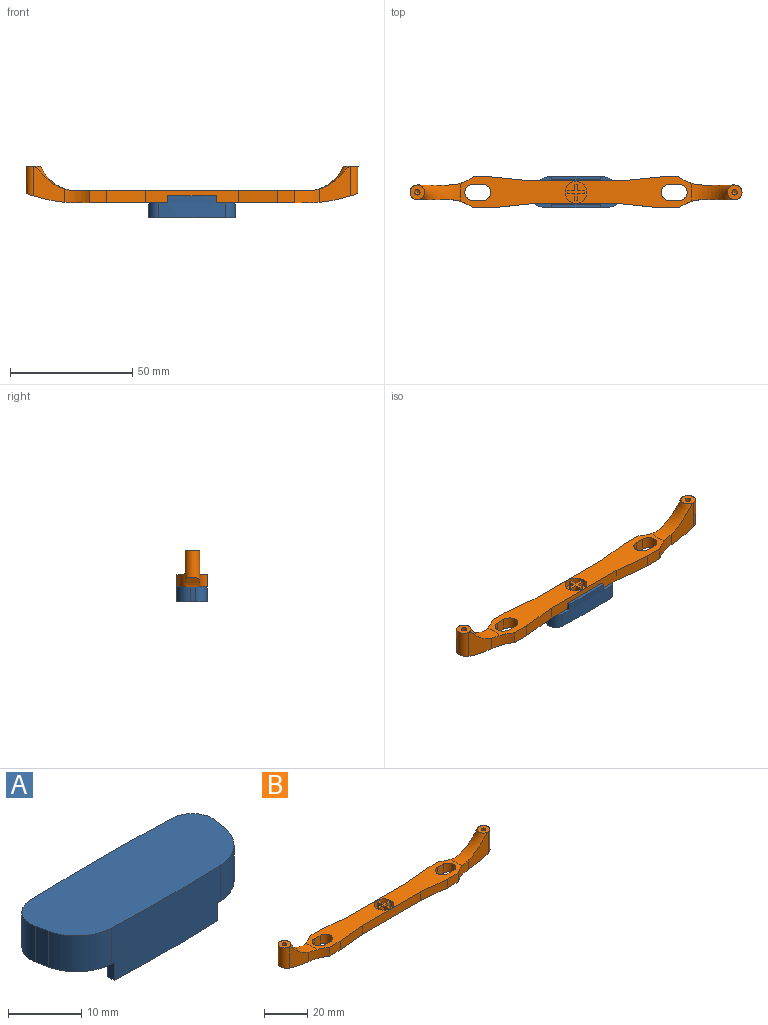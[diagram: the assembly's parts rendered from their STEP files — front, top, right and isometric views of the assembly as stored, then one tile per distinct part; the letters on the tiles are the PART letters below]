
ASSEMBLY  parts=2 mates=1
PART A: 18 faces, bbox 35.3x13x9 mm
  f0: plane 35.26x12.66mm, normal (0,0,-1), area 358.1mm2, adj f1,f2,f3,f4,f5,f6,f7,f8
  f1: plane 6x2.13mm, normal (0.98,-0.2,0), area 13mm2, adj f0,f2,f8,f9
  f2: cylinder r=4mm len=6mm, axis (0,0,-1), area 41.7mm2, adj f0,f1,f3,f9
  f3: cylinder r=342.5mm len=27.58mm, axis (0,0,-1), area 225.5mm2, adj f0,f2,f4,f9,f11,f12,f13
  f4: cylinder r=4mm len=6mm, axis (0,0,-1), area 41.7mm2, adj f0,f3,f5,f9
  f5: plane 6x2.13mm, normal (-0.98,-0.2,0), area 13mm2, adj f0,f4,f6,f9
  f6: cylinder r=7mm len=6.57mm, axis (0,0,-1), area 55.6mm2, adj f0,f5,f7,f9
  f7: cylinder r=256.25mm len=21.07mm, axis (0,0,-1), area 186.5mm2, adj f0,f6,f8,f9,f14,f16,f17
  f8: cylinder r=7mm len=6.57mm, axis (0,0,-1), area 55.6mm2, adj f0,f1,f7,f9
  f9: plane 35.26x13mm, normal (0,0,1), area 415.8mm2, adj f1,f2,f3,f4,f5,f6,f7,f8
  f10: plane 20x3mm, normal (0,-1,0), area 60mm2, adj f0,f11,f12,f13
  f11: plane 3x1.35mm, normal (-1,0,0), area 4.1mm2, adj f0,f3,f10,f13
  f12: plane 3x1.35mm, normal (1,0,0), area 4.1mm2, adj f0,f3,f10,f13
  f13: plane 20x1.5mm, normal (0,0,-1), area 29mm2, adj f3,f10,f11,f12
  f14: plane 3x1.31mm, normal (-1,0,0), area 3.9mm2, adj f0,f7,f15,f17
  f15: plane 20x3mm, normal (0,1,0), area 60mm2, adj f0,f14,f16,f17
  f16: plane 3x1.31mm, normal (1,0,0), area 3.9mm2, adj f0,f7,f15,f17
  f17: plane 20x1.5mm, normal (0,0,-1), area 28.7mm2, adj f7,f14,f15,f16
PART B: 55 faces, bbox 136x63.2x21 mm
  f0: plane 14.74x12.9mm, normal (0,1,0), area 107.7mm2, adj f1,f9,f33,f53
  f1: cylinder r=3mm len=12.06mm, axis (0,0,-1), area 107.4mm2, adj f0,f2,f30,f53
  f2: plane 14.74x12.9mm, normal (0,-1,0), area 107.7mm2, adj f1,f3,f33,f53
  f3: cylinder r=16.5mm len=10mm, axis (0,0,-1), area 54.6mm2, adj f2,f10,f17,f29,f33,f53
  f4: cylinder r=16.5mm len=10mm, axis (0,0,-1), area 54.6mm2, adj f5,f10,f21,f29,f32,f54
  f5: plane 14.74x12.9mm, normal (0,-1,0), area 107.7mm2, adj f4,f6,f32,f54
  f6: cylinder r=3mm len=12.06mm, axis (0,0,-1), area 107.4mm2, adj f5,f7,f31,f54
  f7: plane 14.74x12.9mm, normal (0,1,0), area 107.7mm2, adj f6,f8,f32,f54
  f8: cylinder r=16.5mm len=10mm, axis (0,0,-1), area 54.6mm2, adj f7,f10,f22,f29,f32,f54
  f9: cylinder r=16.5mm len=10mm, axis (0,0,-1), area 54.6mm2, adj f0,f10,f26,f29,f33,f53
  f10: plane 94.76x12.75mm, normal (0,0,-1), area 877.1mm2, adj f3,f4,f8,f9,f11,f12,f13,f14
  f11: plane 5x3.7mm, normal (0,1,0), area 18.5mm2, adj f10,f12,f28,f29
  f12: cylinder r=3.4mm len=6.8mm, axis (0,0,-1), area 53.4mm2, adj f10,f11,f13,f29
  f13: plane 5x3.7mm, normal (0,-1,0), area 18.5mm2, adj f10,f12,f28,f29
  f14: cylinder r=3.4mm len=6.8mm, axis (0,0,-1), area 53.4mm2, adj f10,f15,f27,f29
  f15: plane 5x3.7mm, normal (0,1,0), area 18.5mm2, adj f10,f14,f16,f29
  f16: cylinder r=3.4mm len=6.8mm, axis (0,0,-1), area 53.4mm2, adj f10,f15,f27,f29
  f17: plane 7.1x5mm, normal (0,-1,0), area 35.5mm2, adj f3,f10,f18,f29
  f18: plane 16x5mm, normal (0.1,-0.99,0), area 80.4mm2, adj f10,f17,f19,f29
  f19: plane 38x5mm, normal (0,-1,0), area 190mm2, adj f10,f18,f20,f29
  f20: plane 16x5mm, normal (-0.1,-0.99,0), area 80.4mm2, adj f10,f19,f21,f29
  f21: plane 7.1x5mm, normal (0,-1,0), area 35.5mm2, adj f4,f10,f20,f29
  f22: plane 7.1x5mm, normal (0,1,0), area 35.5mm2, adj f8,f10,f23,f29
  f23: plane 16x5mm, normal (-0.1,0.99,0), area 80.4mm2, adj f10,f22,f24,f29
  f24: plane 38x5mm, normal (0,1,0), area 190mm2, adj f10,f23,f25,f29
  f25: plane 16x5mm, normal (0.1,0.99,0), area 80.4mm2, adj f10,f24,f26,f29
  f26: plane 7.1x5mm, normal (0,1,0), area 35.5mm2, adj f9,f10,f25,f29
  f27: plane 5x3.7mm, normal (0,-1,0), area 18.5mm2, adj f10,f14,f16,f29
  f28: cylinder r=3.4mm len=6.8mm, axis (0,0,-1), area 53.4mm2, adj f10,f11,f13,f29
  f29: plane 95.09x12.75mm, normal (0,0,1), area 812.3mm2, adj f3,f4,f8,f9,f11,f12,f13,f14
  f30: plane 6x6mm, normal (0,0,1), area 24.5mm2, adj f1,f33,f37
  f31: plane 6x6mm, normal (0,0,1), area 24.5mm2, adj f6,f32,f35
  f32: torus R=17.83mm, axis (0,0,1), area 122mm2, adj f4,f5,f7,f8,f29,f31
  f33: torus R=17.83mm, axis (0,0,1), area 122mm2, adj f0,f2,f3,f9,f29,f30
  f34: cone r=0mm half-angle=59deg, axis (0,0,1), area 4.4mm2, adj f35
  f35: cylinder r=1.1mm len=10mm, axis (0,0,1), area 69.1mm2, adj f31,f34
  f36: cone r=0mm half-angle=59deg, axis (0,0,1), area 4.4mm2, adj f37
  f37: cylinder r=1.1mm len=10mm, axis (0,0,1), area 69.1mm2, adj f30,f36
  f38: plane 3x2.8mm, normal (0,1,0), area 8.4mm2, adj f39,f49,f51,f52
  f39: plane 3x2.8mm, normal (-1,0,0), area 8.4mm2, adj f38,f40,f51,f52
  f40: plane 3x1.2mm, normal (0,1,0), area 3.6mm2, adj f39,f41,f51,f52
  f41: plane 3x2.8mm, normal (1,0,0), area 8.4mm2, adj f40,f42,f51,f52
  f42: plane 3x2.8mm, normal (0,1,0), area 8.4mm2, adj f41,f43,f51,f52
  f43: plane 3x1.2mm, normal (1,0,0), area 3.6mm2, adj f42,f44,f51,f52
  f44: plane 3x2.8mm, normal (0,-1,0), area 8.4mm2, adj f43,f45,f51,f52
  f45: plane 3x2.8mm, normal (1,0,0), area 8.4mm2, adj f44,f46,f51,f52
  f46: plane 3x1.2mm, normal (0,-1,0), area 3.6mm2, adj f45,f47,f51,f52
  f47: plane 3x2.8mm, normal (-1,0,0), area 8.4mm2, adj f46,f48,f51,f52
  f48: plane 3x2.8mm, normal (0,-1,0), area 8.4mm2, adj f47,f49,f51,f52
  f49: plane 3x1.2mm, normal (-1,0,0), area 3.6mm2, adj f38,f48,f51,f52
  f50: cylinder r=4.5mm len=9mm, axis (0,0,1), area 84.8mm2, adj f29,f51
  f51: plane 9x9mm, normal (0,0,1), area 48.7mm2, adj f38,f39,f40,f41,f42,f43,f44,f45
  f52: plane 6.8x6.8mm, normal (0,0,1), area 14.9mm2, adj f38,f39,f40,f41,f42,f43,f44,f45
  f53: cylinder r=60mm len=20.62mm, axis (0,-1,0), area 125.8mm2, adj f0,f1,f2,f3,f9,f10
  f54: cylinder r=60mm len=20.62mm, axis (0,-1,0), area 125.8mm2, adj f4,f5,f6,f7,f8,f10
PLACE A rot(axis=(1,0,0),180deg) t=(-19.9,-9.3,1.47)mm
PLACE B t=(-19.9,-9.51,1.47)mm
MATE fastened A.f0 <-> B.f50  axis (0,0,1) through (-19.9,-9.51,1.47)mm
